# Revit family: Safety & Protection_Bollard_UltiGroup_Bollard Rod
name_source: partatom
category: Generic Models
revit_build: Autodesk Revit Architecture 2016 (Build: 20150220_1215(x64)
units: mm (PartAtom-declared; Revit-internal decimal feet)

## family parameters
Always vertical = Yes
Can host rebar = No
Cut with Voids When Loaded = No
OmniClass Number = 23.40.10.14.27
OmniClass Title = Bollards
Part Type = Normal
Room Calculation Point = No
Round Connector Dimension = Use Diameter
Shared = No
Work Plane-Based = No

## types (3) — shared parameters
Aluminium = Aluminium
Bollard Height PE 70 = 266 mm  [stored 0.872703 ft]
Description = Impactable PVC Bollard Rod Type Support
Fax = 07 846 2467
Manufacturer = UltiGroup
PVC Black = PVC Black
PVC Yellow = PVC Yellow
Rod PE 120 radius = 60 mm  [stored 0.19685 ft]
Rod PE 70 radius = 35 mm  [stored 0.114829 ft]
Send Message = http://ultigroup.co.nz
Stainless Steel = Stainless Steel
Support depth = 80 mm  [stored 0.262467 ft]
URL = www.ultigroup.co.nz
zero-valued in all types: InstallationGroup_ANZRS, ModifiedIssue_ANZRS

## per-type parameters (varying)
| type | Bollard Height PE 120 | Model | Rod PE 120 | Rod PE 70 |
| Bollard Rod PE 70 266 RE | 433 mm | Ulti Bollard Rod PE 70 266 RE | No | Yes |
| Bollard Rod PE 120 433 RE | 433 mm | Ulti Bollard Rod PE 120 433 RE | Yes | No |
| Bollard Rod PE 120 560 RE | 560 mm  [stored 1.83727 ft] | Ulti Bollard Rod PE 120 560 RE | Yes | No |

note: [stored X ft] marks values corroborated as IEEE doubles in the binary element streams (Revit-internal decimal feet)

## geometry (parser evidence)
native form markers: Sweep x2
no freeform markers — native parametric forms only
